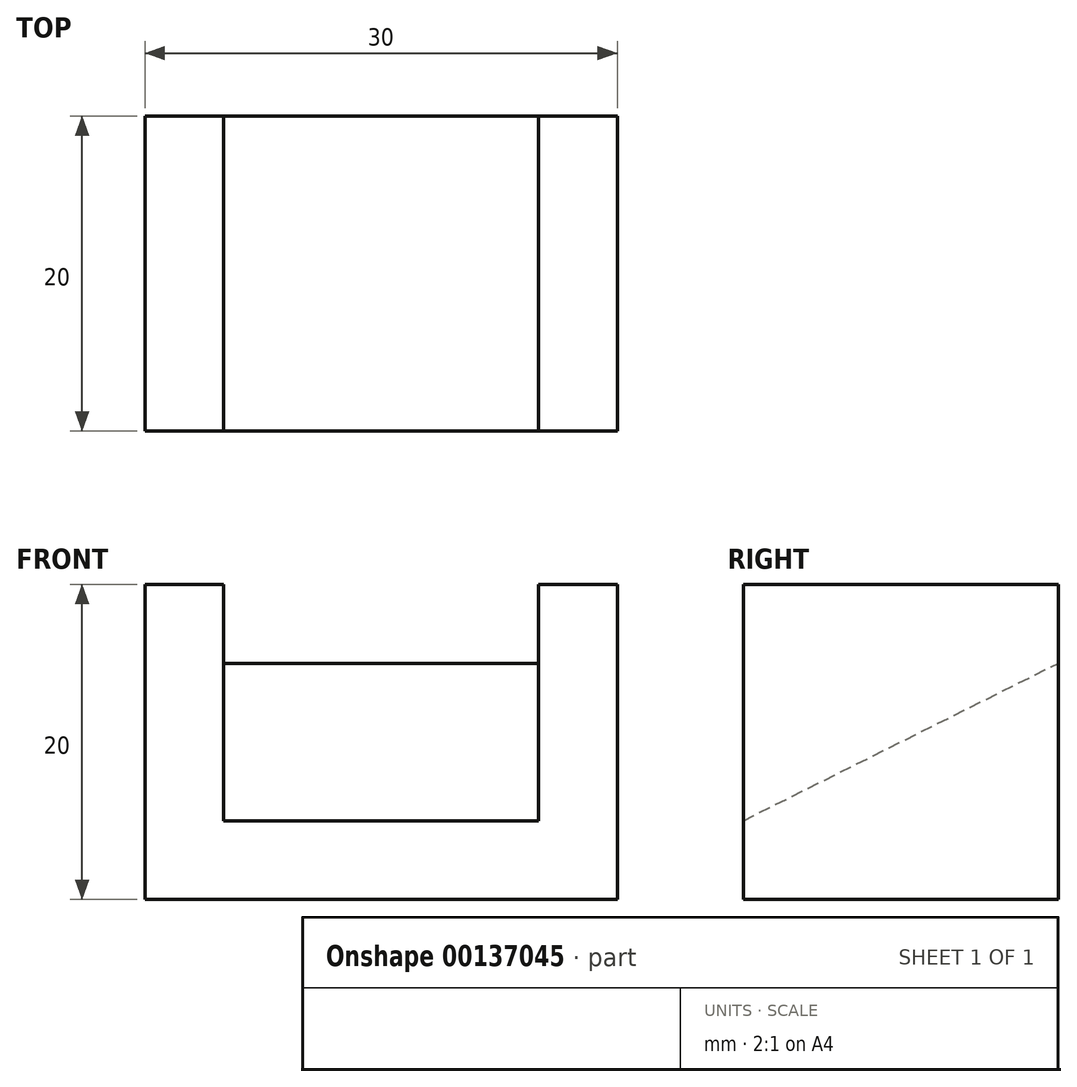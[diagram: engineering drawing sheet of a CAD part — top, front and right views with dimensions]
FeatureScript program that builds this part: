
annotation { "Feature Type Name" : "Feature", "Feature Type Description" : "" }
export const myFeature = defineFeature(function(context is Context, id is Id, definition is map)
    precondition{}
    {
        {
            var Q0;
            Q0=qCreatedBy(makeId("Top.planeOp"),FACE);
            var sketch = newSketch(context, id + "F0", { "sketchPlane" : qUnion([Q0])});
            skLineSegment(sketch, "E0.bottom", {"start": v(0, 0) * mm, "end": v(30, 0) * mm});
            skLineSegment(sketch, "E0.top", {"start": v(0, 20) * mm, "end": v(30, 20) * mm});
            skLineSegment(sketch, "E0.left", {"start": v(0, 0) * mm, "end": v(0, 20) * mm});
            skLineSegment(sketch, "E0.right", {"start": v(30, 0) * mm, "end": v(30, 20) * mm});
            skSolve(sketch);
        }
        {
            var Q0;
            Q0=makeQuery(id+"F0.imprint","IMPRINT",FACE,{"disambiguationData":[TD([[makeQuery(id+"F0.imprint","IMPRINT",EDGE,{"derivedFrom":sQuery(id+"F0.wireOp",EDGE,"E0.bottom")}),1.0]])]});
            extrude(context, id + "F1", {"entities" : qUnion([Q0]), "depth" : 20 * mm});
        }
        {
            var Q0;
            Q0=qCreatedBy(makeId("Right.planeOp"),FACE);
            var sketch = newSketch(context, id + "F2", { "sketchPlane" : qUnion([Q0])});
            skLineSegment(sketch, "E1.bottom", {"start": v(0, 0) * mm, "end": v(20, 0) * mm});
            skLineSegment(sketch, "E1.top", {"start": v(0, 20) * mm, "end": v(20, 20) * mm});
            skLineSegment(sketch, "E1.left", {"start": v(0, 0) * mm, "end": v(0, 20) * mm});
            skLineSegment(sketch, "E1.right", {"start": v(20, 0) * mm, "end": v(20, 20) * mm});
            skLineSegment(sketch, "E2", {"start": v(0, 5) * mm, "end": v(20, 15) * mm});
            skLineSegment(sketch, "E3", {"start": v(0, 0) * mm, "end": v(0, 5) * mm});
            skLineSegment(sketch, "E4", {"start": v(20, 15) * mm, "end": v(20, 20) * mm});
            skLineSegment(sketch, "E5", {"start": v(0, 5) * mm, "end": v(0, 20) * mm});
            skSolve(sketch);
        }
        {
            var Q0;
            Q0=makeQuery(id+"F2.imprint","IMPRINT",FACE,{"disambiguationData":[TD([[makeQuery(id+"F2.imprint","IMPRINT",EDGE,{"derivedFrom":sQuery(id+"F2.wireOp",EDGE,"E1.top")}),-1.0]])]});
            var Q1;
            Q1=sQuery(id+"F2.wireOp",EDGE,"E1.top");
            var Q2;
            Q2=sQuery(id+"F2.wireOp",EDGE,"E2");
            var Q3;
            Q3=sQuery(id+"F2.wireOp",EDGE,"E5");
            var Q4;
            Q4=sQuery(id+"F2.wireOp",EDGE,"E4");
            extrude(context, id + "F3", {"entities" : qUnion([Q0]), "operationType" : NewBodyOperationType.REMOVE, "surfaceEntities" : qUnion([Q1, Q2, Q3, Q4]), "depth" : 25 * mm, "hasSecondDirection" : true, "secondDirectionOppositeDirection" : false, "secondDirectionDepth" : 5 * mm});
        }
    });
